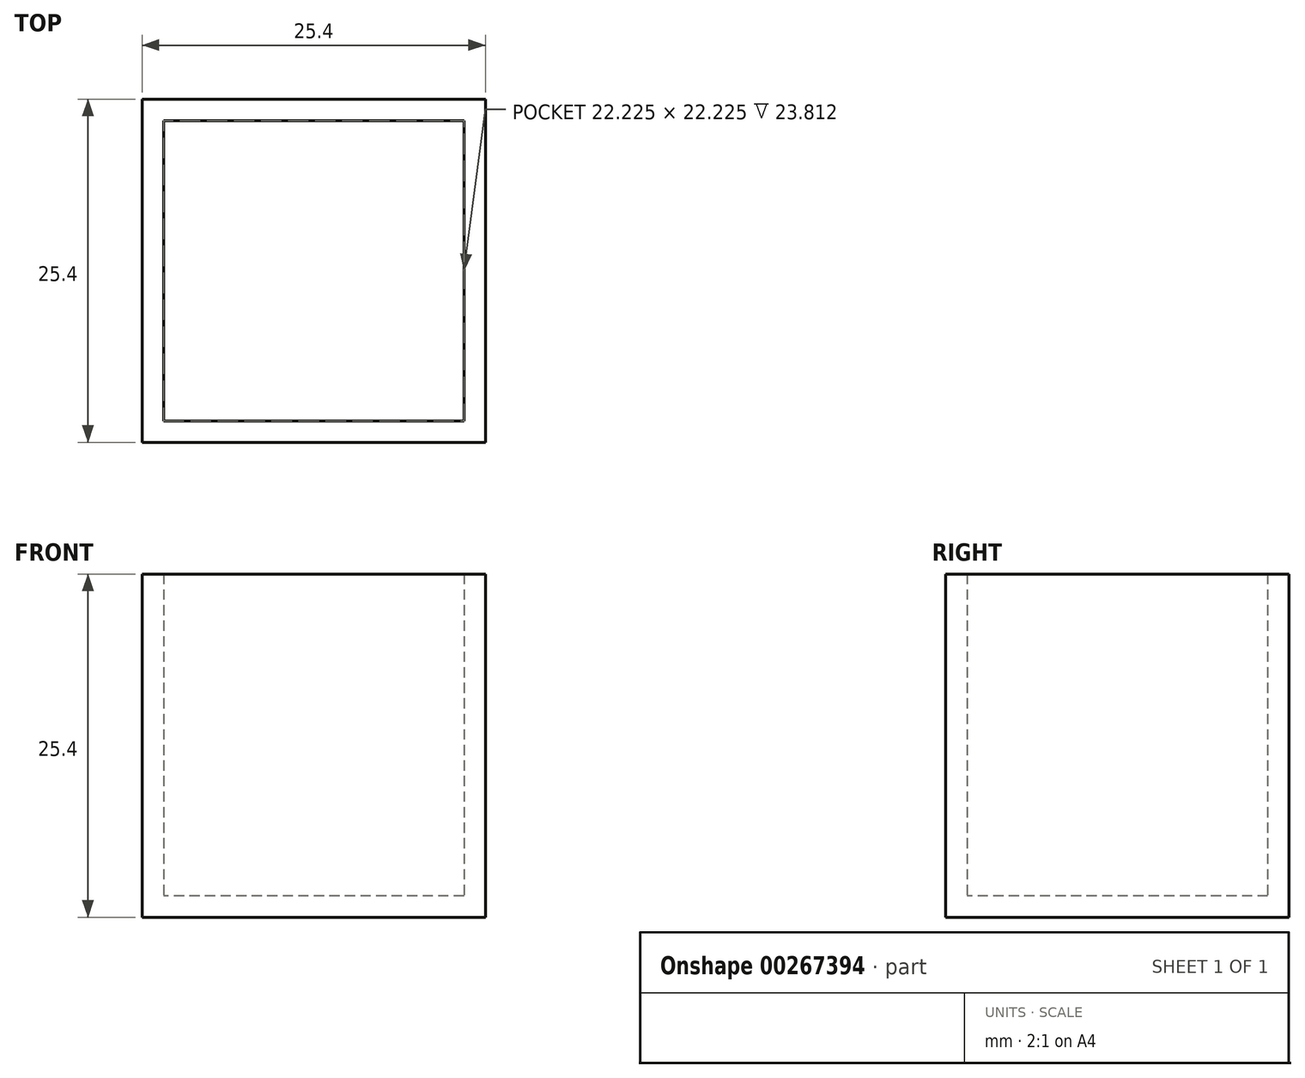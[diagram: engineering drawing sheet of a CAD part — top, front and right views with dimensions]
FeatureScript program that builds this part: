
annotation { "Feature Type Name" : "Feature", "Feature Type Description" : "" }
export const myFeature = defineFeature(function(context is Context, id is Id, definition is map)
    precondition{}
    {
        {
            var Q0;
            Q0=qCreatedBy(makeId("Top.planeOp"),FACE);
            var sketch = newSketch(context, id + "F0", { "sketchPlane" : qUnion([Q0])});
            skLineSegment(sketch, "E0.bottom", {"start": v(12.7, 12.7) * mm, "end": v(-12.7, 12.7) * mm});
            skLineSegment(sketch, "E0.top", {"start": v(12.7, -12.7) * mm, "end": v(-12.7, -12.7) * mm});
            skLineSegment(sketch, "E0.left", {"start": v(12.7, 12.7) * mm, "end": v(12.7, -12.7) * mm});
            skLineSegment(sketch, "E0.right", {"start": v(-12.7, 12.7) * mm, "end": v(-12.7, -12.7) * mm});
            skPoint(sketch, "E0.middle", {"position": v(0, 0) * mm});
            skSolve(sketch);
        }
        {
            var Q0;
            Q0=qSketchRegion(id+"F0",true);
            extrude(context, id + "F1", {"entities" : qUnion([Q0]), "depth" : 1.59 * mm});
        }
        {
            var Q0;
            Q0=makeQuery(id+"F1.opExtrude","CAP_FACE",FACE,{"disambiguationData":[OSD([sQuery(id+"F0.wireOp",EDGE,"E0.bottom"),sQuery(id+"F0.wireOp",EDGE,"E0.top"),sQuery(id+"F0.wireOp",EDGE,"E0.left"),sQuery(id+"F0.wireOp",EDGE,"E0.right")])],"isStart":false});
            var sketch = newSketch(context, id + "F2", { "sketchPlane" : qUnion([Q0])});
            skLineSegment(sketch, "E1.bottom", {"start": v(11.11, 11.11) * mm, "end": v(-11.11, 11.11) * mm});
            skLineSegment(sketch, "E1.top", {"start": v(11.11, -11.11) * mm, "end": v(-11.11, -11.11) * mm});
            skLineSegment(sketch, "E1.left", {"start": v(11.11, 11.11) * mm, "end": v(11.11, -11.11) * mm});
            skLineSegment(sketch, "E1.right", {"start": v(-11.11, 11.11) * mm, "end": v(-11.11, -11.11) * mm});
            skPoint(sketch, "E1.middle", {"position": v(0, 0) * mm});
            skLineSegment(sketch, "E2.bottom", {"start": v(12.7, 12.7) * mm, "end": v(-12.7, 12.7) * mm});
            skLineSegment(sketch, "E2.top", {"start": v(12.7, -12.7) * mm, "end": v(-12.7, -12.7) * mm});
            skLineSegment(sketch, "E2.left", {"start": v(12.7, 12.7) * mm, "end": v(12.7, -12.7) * mm});
            skLineSegment(sketch, "E2.right", {"start": v(-12.7, 12.7) * mm, "end": v(-12.7, -12.7) * mm});
            skCircle(sketch, "E3", {"center": v(0, 0) * mm, "radius": 0.13 * mm});
            skSolve(sketch);
        }
        {
            var Q0;
            Q0=qSketchRegion(id+"F2",true);
            extrude(context, id + "F3", {"entities" : qUnion([Q0]), "operationType" : NewBodyOperationType.ADD, "depth" : 23.8 * mm});
        }
    });
